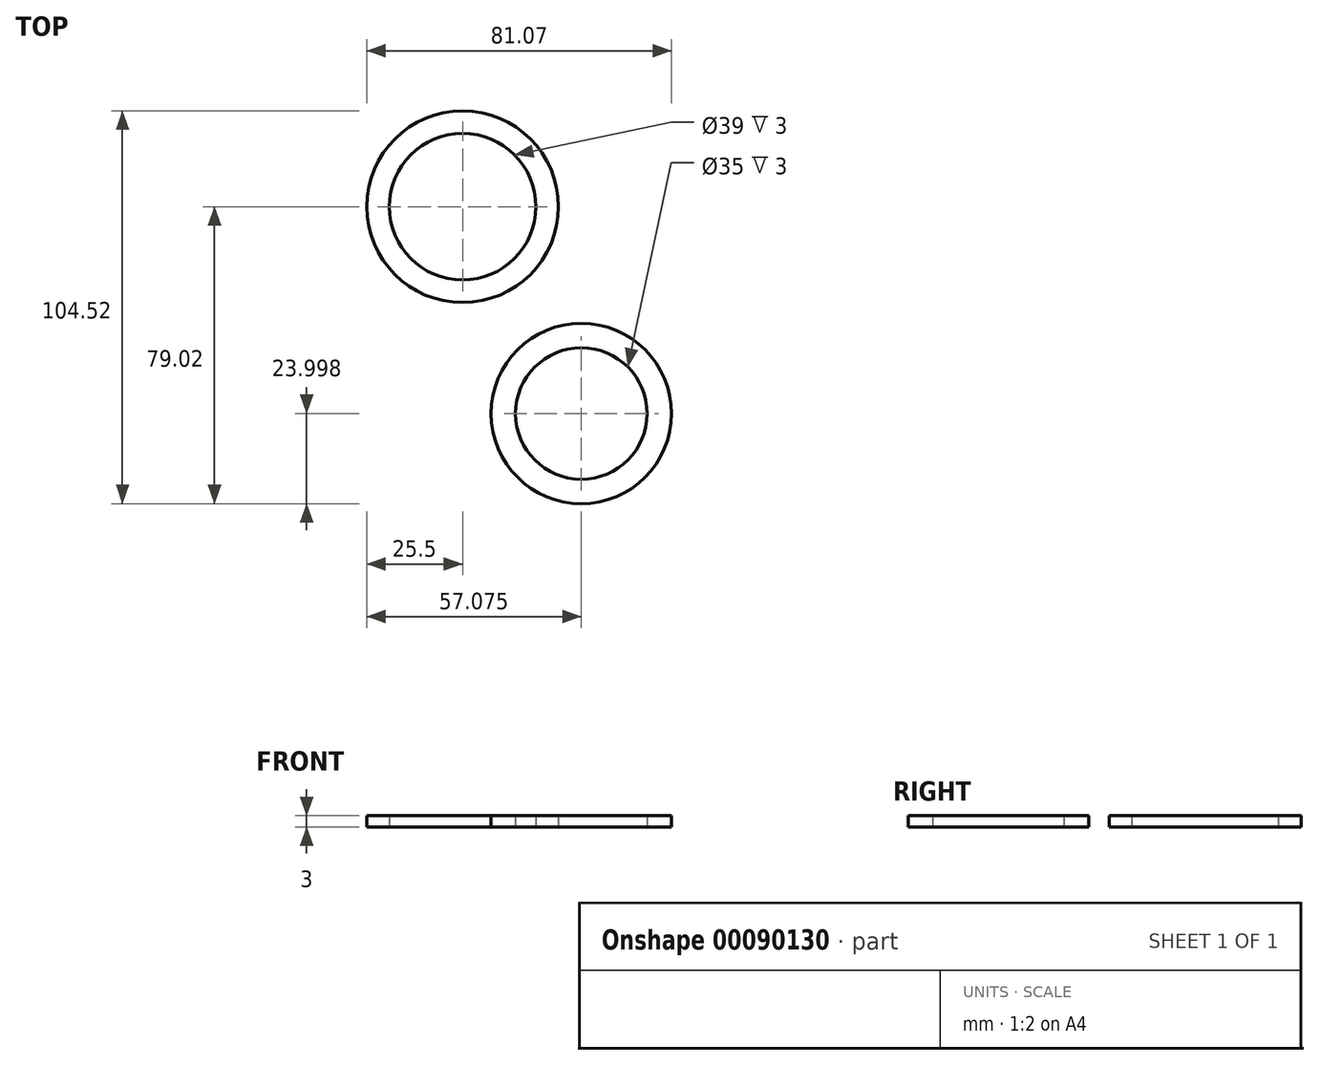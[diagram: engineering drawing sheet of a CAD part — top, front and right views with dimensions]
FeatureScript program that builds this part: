
annotation { "Feature Type Name" : "Feature", "Feature Type Description" : "" }
export const myFeature = defineFeature(function(context is Context, id is Id, definition is map)
    precondition{}
    {
        {
            var Q0;
            Q0=qCreatedBy(makeId("Top.planeOp"),FACE);
            var sketch = newSketch(context, id + "F0", { "sketchPlane" : qUnion([Q0])});
            skCircle(sketch, "E0", {"center": v(0, 0) * mm, "radius": 19.5 * mm});
            skCircle(sketch, "E1", {"center": v(0, 0) * mm, "radius": 25.5 * mm});
            skCircle(sketch, "E2", {"center": v(31.57, -55.02) * mm, "radius": 17.5 * mm});
            skCircle(sketch, "E3", {"center": v(31.57, -55.02) * mm, "radius": 24 * mm});
            skSolve(sketch);
        }
        {
            var Q0;
            Q0 = qSketchRegion(id + "F0", true);
            extrude(context, id + "F1", {"entities" : qUnion([Q0]), "depth" : 3 * mm});
        }
    });
